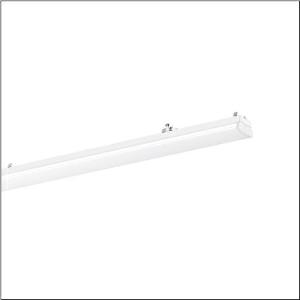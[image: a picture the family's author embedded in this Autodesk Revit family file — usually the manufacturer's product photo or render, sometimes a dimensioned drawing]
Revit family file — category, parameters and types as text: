
# Revit family: licross_21_recessed_opal_mo_52tl1d7n46xg
name_source: partatom
category: Lighting Fixtures
units: mm (PartAtom-declared; Revit-internal decimal feet)

## family parameters
Cut with Voids When Loaded = No
Host = Face
Light Source = No
Part Type = Normal
Room Calculation Point = No
Round Connector Dimension = Use Diameter
Shared = No

## types (1)
- Licross 21 recessed opal MO (1 x LED, 6200 lm, 34.9 W, 4000K)
    Apparent Load = 35 VA
    CIE Flux Codes = 44 73 91 87 100
    Color Rendering = 80
    Color Temperature = 4000K
    Default Elevation = 1800 mm
    Description = Licross 21 recessed opal MO, luminaire insert, of sheet steel, galvanised, coil coated, white, length: 1.500mm, width: 66mm, height: 67mm, LED rated luminous flux: 6.200lm, light colour: 840, SDCM (Standard Deviation of Colour Matching)MacAdam ≤ 3 SDCM (initial), control gear: ON/OFF, with plug, 3-pole, with phase selection, mains connection: 220..240V, AC, 50/60Hz, rated input power: 35W, internal wiring halogen-free, primary optical cover: cover, of PMMA, light emission: direct with ceiling illumination distribution, primary light characteristic: symmetric, protection rating (complete): IP40, insulation class (complete): insulation class I (protective earthing), certification: CE, ENEC, VDE, UKCA, protection symbol: D if used in an environment without relevant dust loads with corresponding accessories, impact resistance: IK06, permissible ambient temperature for indoor applications: -35..+50°C, corresponds to IFS (International Featured Standards) requirements for safety and quality in the food industry, reducing of maximum allowable ambient temperature of 5°C with ceiling mounting, LABS conformity tested according to VDMA 24364:2018-05, The light source and the operating device comply with the requirements of the Ecodesign Regulation (EU) 2019/2020 and are replaceable in accordance with this regulation, packaging unit: 1 piece
    Height = 83 mm
    Lamp = 1 x LED
    Lamp Light Flux = 6200 lm
    Lamp Power = 34.9 W
    Lamp count = 1
    Length = 1500 mm
    Luminous efficacy = 178 lm/W
    Manufacturer = Siteco
    ModVariant = No
    Model = 52TL1D7N46XG
    Mounting Place = Ceiling
    Mounting Type = Pendant
    Number of Poles = 1
    OnlyDefault = Yes
    Power Factor = 1
    Product Name = Licross 21 recessed opal MO
    Product group = luminaire insert | ceiling pendant
    ProductGroupID = 901
    Protection Class = Protection class I
    Protection Degree = IP 40
    RLX_Detail_Level = 1
    RLX_Emergency_Light_Flux = 0 lm
    RLX_Emergency_Type = 0
    RLX_Emergency_Type_DB = No
    RlxData = <blob elided: 23361 chars, md5=98f71ad1>
    Socket = socket
    Standby Power = 0 W
    System Light Flux = 6200 lm
    System Power = 35 W
    Type Comments = Product without accessories
    Type Image = l_1313666.jpg
    URL = http://relux.com
    VarID = ---
    Voltage = 0 V
    Weight = 0.00 kg
    Width = 76 mm

## geometry (parser evidence)
native form markers: Blend x4, Sweep x12
no freeform markers — native parametric forms only
